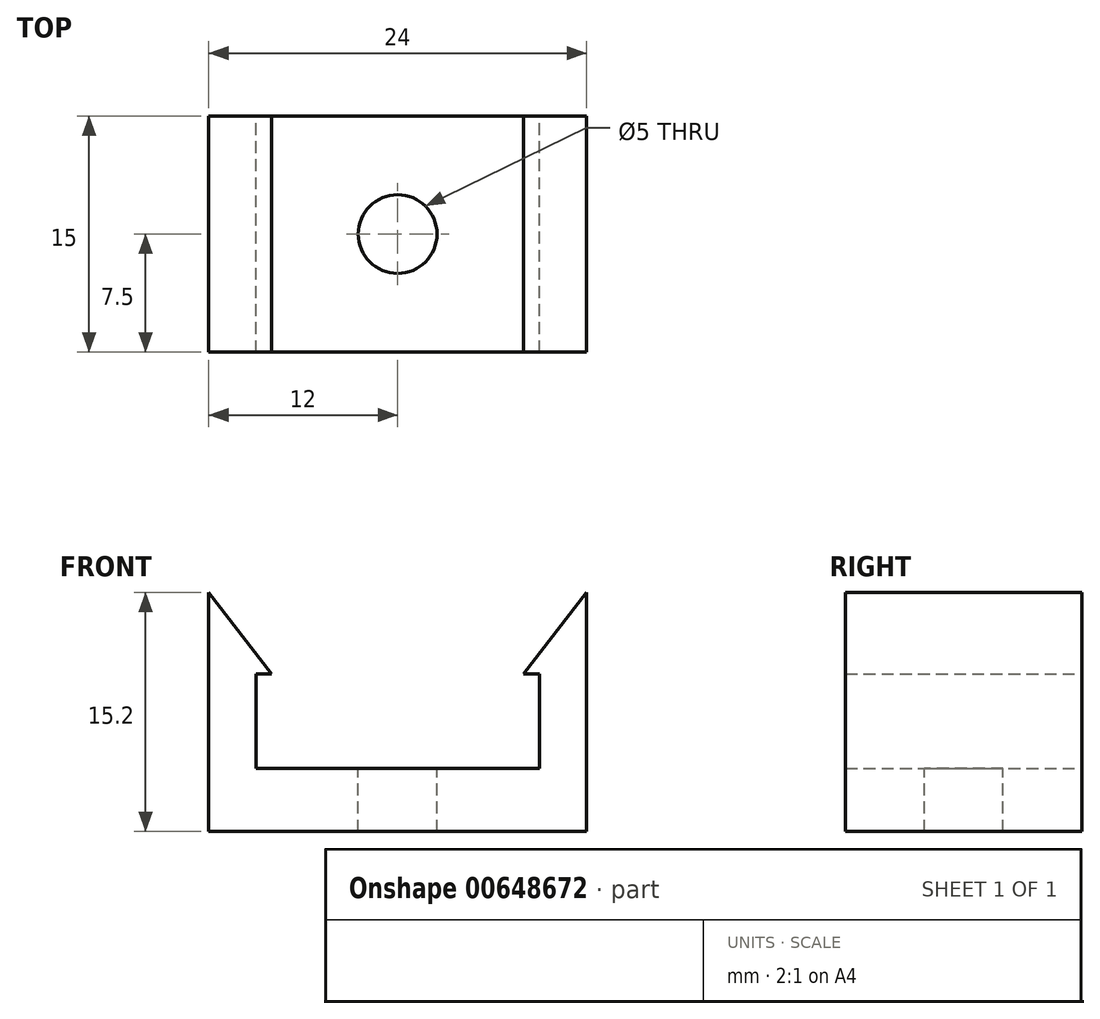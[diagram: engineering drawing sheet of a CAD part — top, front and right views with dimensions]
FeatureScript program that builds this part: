
annotation { "Feature Type Name" : "Feature", "Feature Type Description" : "" }
export const myFeature = defineFeature(function(context is Context, id is Id, definition is map)
    precondition{}
    {
        {
            var Q0;
            Q0=qCreatedBy(makeId("Front.planeOp"),FACE);
            var sketch = newSketch(context, id + "F0", { "sketchPlane" : qUnion([Q0])});
            skLineSegment(sketch, "E0", {"start": v(12, 0) * mm, "end": v(12, 15.2) * mm});
            skLineSegment(sketch, "E1", {"start": v(12, 15.2) * mm, "end": v(8, 10) * mm});
            skLineSegment(sketch, "E2", {"start": v(8, 10) * mm, "end": v(9, 10) * mm});
            skLineSegment(sketch, "E3", {"start": v(9, 10) * mm, "end": v(9, 4) * mm});
            skLineSegment(sketch, "E4", {"start": v(9, 4) * mm, "end": v(0, 4) * mm});
            skLineSegment(sketch, "E5", {"start": v(12, 0) * mm, "end": v(0, 0) * mm});
            skLineSegment(sketch, "E6", {"start": v(0, 4) * mm, "end": v(0, 0) * mm});
            skSolve(sketch);
        }
        {
            var Q0;
            Q0 = qSketchRegion(id + "F0", true);
            extrude(context, id + "F1", {"entities" : qUnion([Q0]), "depth" : 15 * mm, "offsetDistance" : 25 * mm});
        }
        {
            var Q0;
            Q0=makeQuery(id+"F1.opExtrude","SWEPT_BODY",BODY,{"disambiguationData":[OSD([sQuery(id+"F0.wireOp",EDGE,"E0"),sQuery(id+"F0.wireOp",EDGE,"E1"),sQuery(id+"F0.wireOp",EDGE,"E2"),sQuery(id+"F0.wireOp",EDGE,"E3"),sQuery(id+"F0.wireOp",EDGE,"E4"),sQuery(id+"F0.wireOp",EDGE,"E5"),sQuery(id+"F0.wireOp",EDGE,"E6")])]});
            var Q1;
            Q1=makeQuery(id+"F1.opExtrude","SWEPT_FACE",FACE,{"disambiguationData":[OSD([sQuery(id+"F0.wireOp",EDGE,"E6")])]});
            mirror(context, id + "F2", {"operationType" : NewBodyOperationType.ADD, "entities" : qUnion([Q0]), "mirrorPlane" : qUnion([Q1])});
        }
        {
            var Q0;
            {var subQ0=makeQuery(id+"F1.opExtrude","SWEPT_FACE",FACE,{"disambiguationData":[OSD([sQuery(id+"F0.wireOp",EDGE,"E4")])]});Q0=makeQuery(id+"F2.boolean.opBoolean","MERGE",FACE,{"derivedFrom":[subQ0,makeQuery(id+"F2.opPattern","COPY",FACE,{"derivedFrom":subQ0,"instanceName":"1"})]});}
            var sketch = newSketch(context, id + "F3", { "sketchPlane" : qUnion([Q0])});
            skCircle(sketch, "E7", {"center": v(0, -7.5) * mm, "radius": 2.5 * mm});
            skSolve(sketch);
        }
        {
            var Q0;
            Q0=sQuery(id+"F3.wireOp",VERTEX,"E7.center");
            var Q1;
            Q1=makeQuery(id+"F1.opExtrude","SWEPT_BODY",BODY,{"disambiguationData":[OSD([sQuery(id+"F0.wireOp",EDGE,"E0"),sQuery(id+"F0.wireOp",EDGE,"E1"),sQuery(id+"F0.wireOp",EDGE,"E2"),sQuery(id+"F0.wireOp",EDGE,"E3"),sQuery(id+"F0.wireOp",EDGE,"E4"),sQuery(id+"F0.wireOp",EDGE,"E5"),sQuery(id+"F0.wireOp",EDGE,"E6")])]});
            hole(context, id + "F4", {"style" : HoleStyle.SIMPLE, "endStyle" : HoleEndStyle.THROUGH, "holeDiameter" : 5 * mm, "majorDiameter" : 5 * mm, "isTappedThrough" : true, "tappedDepth" : 12 * mm, "tapClearance" : 3, "locations" : qUnion([Q0]), "scope" : qUnion([Q1])});
        }
    });
